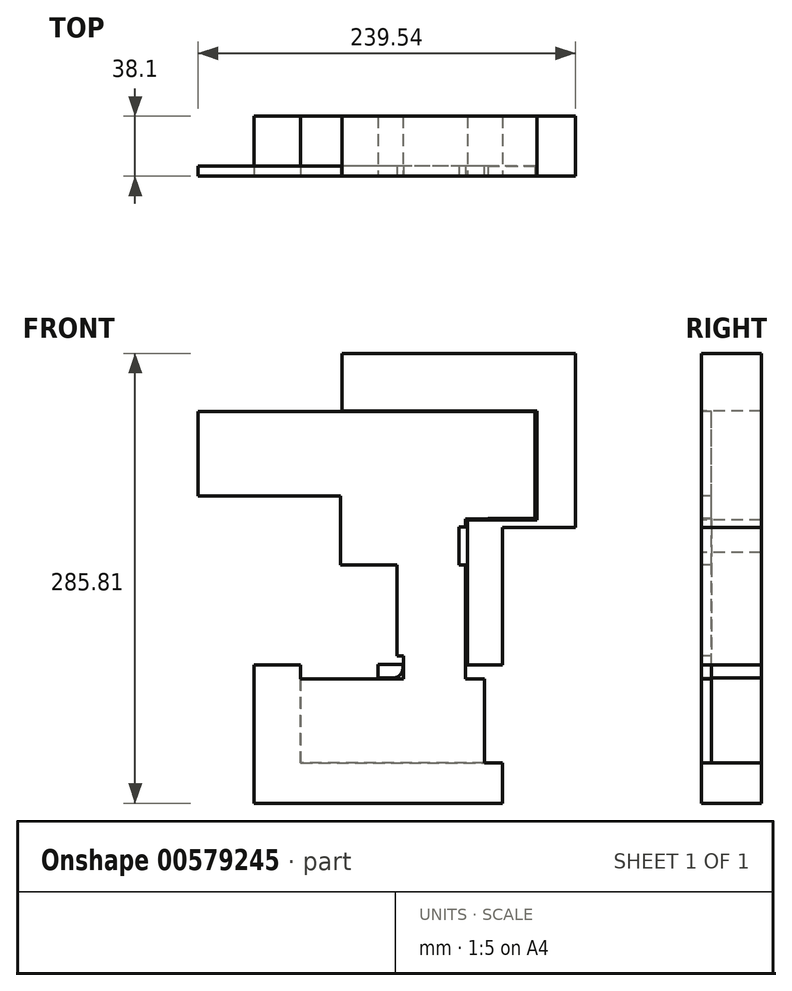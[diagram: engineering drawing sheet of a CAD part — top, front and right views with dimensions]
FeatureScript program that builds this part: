
annotation { "Feature Type Name" : "Feature", "Feature Type Description" : "" }
export const myFeature = defineFeature(function(context is Context, id is Id, definition is map)
    precondition{}
    {
        {
            var Q0;
            Q0=qCreatedBy(makeId("Front.planeOp"),FACE);
            var sketch = newSketch(context, id + "F0", { "sketchPlane" : qUnion([Q0])});
            skLineSegment(sketch, "E0.left", {"start": v(90.58, 112.71) * mm, "end": v(90.58, 180.76) * mm});
            skLineSegment(sketch, "E1.MirrorCS", {"start": v(58.51, 10.86) * mm, "end": v(46.44, 10.86) * mm});
            skLineSegment(sketch, "E2.MirrorCS", {"start": v(46.44, 107.59) * mm, "end": v(42.23, 107.59) * mm});
            skLineSegment(sketch, "E3.MirrorCS", {"start": v(46.44, 112.71) * mm, "end": v(46.44, 107.59) * mm});
            skLineSegment(sketch, "E4.MirrorCS", {"start": v(60.61, 112.71) * mm, "end": v(46.44, 112.46) * mm});
            skLineSegment(sketch, "E5.MirrorCS", {"start": v(42.23, 107.59) * mm, "end": v(46.44, 107.59) * mm});
            skLineSegment(sketch, "E6.MirrorCS", {"start": v(7.13, 10.86) * mm, "end": v(46.44, 10.86) * mm});
            skLineSegment(sketch, "E7.MirrorCS", {"start": v(2.75, 83.2) * mm, "end": v(7.13, 83.2) * mm});
            skLineSegment(sketch, "E8.MirrorCS", {"start": v(46.44, 10.86) * mm, "end": v(7.13, 10.86) * mm});
            skLineSegment(sketch, "E9.MirrorCS", {"start": v(7.13, 25.59) * mm, "end": v(2.75, 25.59) * mm});
            skLineSegment(sketch, "E10.MirrorCS", {"start": v(46.44, 10.86) * mm, "end": v(2.75, 10.86) * mm});
            skLineSegment(sketch, "E11.MirrorCS", {"start": v(7.13, 10.86) * mm, "end": v(7.13, 25.59) * mm});
            skLineSegment(sketch, "E12.MirrorCS", {"start": v(-33.11, 112.71) * mm, "end": v(-33.11, 180.76) * mm});
            skLineSegment(sketch, "E13.MirrorCS", {"start": v(-33.11, 112.71) * mm, "end": v(90.58, 112.71) * mm});
            skLineSegment(sketch, "E14.MirrorCS", {"start": v(-33.11, 127.22) * mm, "end": v(-118.78, 127.22) * mm});
            skLineSegment(sketch, "E15.MirrorCS", {"start": v(2.75, 83.2) * mm, "end": v(-33.11, 83.2) * mm});
            skLineSegment(sketch, "E16.MirrorCS", {"start": v(46.44, 10.86) * mm, "end": v(46.44, 10.86) * mm});
            skLineSegment(sketch, "E17.MirrorCS", {"start": v(2.75, 83.2) * mm, "end": v(2.75, 25.59) * mm});
            skLineSegment(sketch, "E18.MirrorCS", {"start": v(-33.11, 112.71) * mm, "end": v(42.23, 112.71) * mm});
            skLineSegment(sketch, "E19.MirrorCS", {"start": v(90.58, 180.76) * mm, "end": v(-123.38, 180.76) * mm});
            skLineSegment(sketch, "E20.MirrorCS", {"start": v(7.13, 112.46) * mm, "end": v(46.44, 112.46) * mm});
            skLineSegment(sketch, "E21.MirrorCS", {"start": v(-123.38, 127.22) * mm, "end": v(-33.11, 127.22) * mm});
            skLineSegment(sketch, "E22.MirrorCS", {"start": v(-123.38, 127.22) * mm, "end": v(-123.38, 180.76) * mm});
            skLineSegment(sketch, "E23.MirrorCS", {"start": v(-58.33, 10.86) * mm, "end": v(58.51, 10.86) * mm});
            skLineSegment(sketch, "E24.MirrorCS", {"start": v(-58.33, -42.48) * mm, "end": v(-58.33, 10.86) * mm});
            skLineSegment(sketch, "E25.MirrorCS", {"start": v(7.13, 10.86) * mm, "end": v(7.13, 10.86) * mm});
            skLineSegment(sketch, "E26.MirrorCS", {"start": v(-33.11, 83.2) * mm, "end": v(46.44, 83.2) * mm});
            skLineSegment(sketch, "E27.MirrorCS", {"start": v(-33.11, 180.76) * mm, "end": v(-33.11, 112.71) * mm});
            skLineSegment(sketch, "E28.MirrorCS", {"start": v(46.44, 10.86) * mm, "end": v(46.44, 83.2) * mm});
            skLineSegment(sketch, "E29.MirrorCS", {"start": v(46.44, 112.71) * mm, "end": v(2.75, 112.71) * mm});
            skLineSegment(sketch, "E30.MirrorCS", {"start": v(42.23, 112.71) * mm, "end": v(42.23, 83.2) * mm});
            skLineSegment(sketch, "E31.MirrorCS", {"start": v(7.13, 10.86) * mm, "end": v(7.13, 112.46) * mm});
            skLineSegment(sketch, "E32.MirrorCS", {"start": v(-33.11, 83.2) * mm, "end": v(-33.11, 112.71) * mm});
            skLineSegment(sketch, "E33.MirrorCS", {"start": v(-58.33, -42.48) * mm, "end": v(58.51, -42.48) * mm});
            skLineSegment(sketch, "E34", {"start": v(58.51, 10.86) * mm, "end": v(58.51, -42.48) * mm});
            skSolve(sketch);
        }
        {
            var Q0;
            Q0=qCreatedBy(makeId("Front.planeOp"),FACE);
            var sketch = newSketch(context, id + "F1", { "sketchPlane" : qUnion([Q0])});
            skLineSegment(sketch, "E35.bottom", {"start": v(-32.1, 181.22) * mm, "end": v(92.03, 181.22) * mm});
            skLineSegment(sketch, "E35.top", {"start": v(-32.1, 217.68) * mm, "end": v(92.03, 217.68) * mm});
            skLineSegment(sketch, "E35.left", {"start": v(-32.1, 181.22) * mm, "end": v(-32.1, 217.68) * mm});
            skLineSegment(sketch, "E35.right", {"start": v(92.03, 181.22) * mm, "end": v(92.03, 217.68) * mm});
            skLineSegment(sketch, "E36.bottom", {"start": v(47.76, 91.29) * mm, "end": v(69.82, 91.29) * mm});
            skLineSegment(sketch, "E36.top", {"start": v(47.76, 107.02) * mm, "end": v(69.82, 107.02) * mm});
            skLineSegment(sketch, "E36.left", {"start": v(47.76, 91.29) * mm, "end": v(47.76, 107.02) * mm});
            skLineSegment(sketch, "E36.right", {"start": v(69.82, 91.29) * mm, "end": v(69.82, 107.02) * mm});
            skLineSegment(sketch, "E37.bottom", {"start": v(47.72, 19.77) * mm, "end": v(69.82, 19.77) * mm});
            skLineSegment(sketch, "E37.top", {"start": v(47.72, 91.29) * mm, "end": v(69.82, 91.29) * mm});
            skLineSegment(sketch, "E37.left", {"start": v(47.72, 19.77) * mm, "end": v(47.72, 91.29) * mm});
            skLineSegment(sketch, "E37.right", {"start": v(69.82, 19.77) * mm, "end": v(69.82, 91.29) * mm});
            skLineSegment(sketch, "E38.bottom", {"start": v(58.77, 19.77) * mm, "end": v(69.82, 19.77) * mm});
            skLineSegment(sketch, "E38.top", {"start": v(58.77, -42.45) * mm, "end": v(69.82, -42.45) * mm});
            skLineSegment(sketch, "E38.left", {"start": v(58.77, 19.77) * mm, "end": v(58.77, -42.45) * mm});
            skLineSegment(sketch, "E38.right", {"start": v(69.82, 19.77) * mm, "end": v(69.82, -42.45) * mm});
            skLineSegment(sketch, "E39.bottom", {"start": v(69.82, -42.45) * mm, "end": v(-58.3, -42.45) * mm});
            skLineSegment(sketch, "E39.top", {"start": v(69.82, -68.05) * mm, "end": v(-58.3, -68.05) * mm});
            skLineSegment(sketch, "E39.left", {"start": v(69.82, -42.45) * mm, "end": v(69.82, -68.05) * mm});
            skLineSegment(sketch, "E39.right", {"start": v(-58.3, -42.45) * mm, "end": v(-58.3, -68.05) * mm});
            skLineSegment(sketch, "E40.bottom", {"start": v(-58.3, -68.05) * mm, "end": v(-87.9, -68.05) * mm});
            skLineSegment(sketch, "E40.top", {"start": v(-58.3, 19.77) * mm, "end": v(-87.9, 19.77) * mm});
            skLineSegment(sketch, "E40.left", {"start": v(-58.3, -68.05) * mm, "end": v(-58.3, 19.77) * mm});
            skLineSegment(sketch, "E40.right", {"start": v(-87.9, -68.05) * mm, "end": v(-87.9, 19.77) * mm});
            skLineSegment(sketch, "E41.bottom", {"start": v(0.3, 11.52) * mm, "end": v(-9.1, 11.52) * mm});
            skLineSegment(sketch, "E41.top", {"start": v(6.65, 20.04) * mm, "end": v(-9.1, 20.04) * mm});
            skLineSegment(sketch, "E41.left", {"start": v(6.65, 17.87) * mm, "end": v(6.65, 20.04) * mm});
            skLineSegment(sketch, "E41.right", {"start": v(-9.1, 11.52) * mm, "end": v(-9.1, 20.04) * mm});
            skLineSegment(sketch, "E42.bottom", {"start": v(2.21, 20.04) * mm, "end": v(-9.1, 20.04) * mm});
            skLineSegment(sketch, "E42.top", {"start": v(2.21, 76.37) * mm, "end": v(-9.1, 76.37) * mm});
            skLineSegment(sketch, "E42.left", {"start": v(2.21, 20.04) * mm, "end": v(2.21, 76.37) * mm});
            skLineSegment(sketch, "E42.right", {"start": v(-9.1, 20.04) * mm, "end": v(-9.1, 76.37) * mm});
            skLineSegment(sketch, "E43.bottom", {"start": v(-9.1, 11.52) * mm, "end": v(-87.9, 11.52) * mm});
            skLineSegment(sketch, "E43.left", {"start": v(-9.1, 11.52) * mm, "end": v(-9.1, 25.06) * mm});
            skLineSegment(sketch, "E44.bottom", {"start": v(47.67, 107.02) * mm, "end": v(116.16, 107.02) * mm});
            skLineSegment(sketch, "E44.top", {"start": v(47.67, 111.94) * mm, "end": v(116.16, 111.94) * mm});
            skLineSegment(sketch, "E44.left", {"start": v(47.67, 107.02) * mm, "end": v(47.67, 111.94) * mm});
            skLineSegment(sketch, "E44.right", {"start": v(116.16, 107.02) * mm, "end": v(116.16, 111.94) * mm});
            skLineSegment(sketch, "E45.bottom", {"start": v(91.87, 111.94) * mm, "end": v(116.16, 111.94) * mm});
            skLineSegment(sketch, "E45.top", {"start": v(91.87, 217.76) * mm, "end": v(116.16, 217.76) * mm});
            skLineSegment(sketch, "E45.left", {"start": v(91.87, 111.94) * mm, "end": v(91.87, 217.76) * mm});
            skLineSegment(sketch, "E45.right", {"start": v(116.16, 111.94) * mm, "end": v(116.16, 217.76) * mm});
            skLineSegment(sketch, "E46.bottom", {"start": v(116.16, 107.02) * mm, "end": v(69.82, 107.02) * mm});
            skLineSegment(sketch, "E46.top", {"start": v(116.16, -68.05) * mm, "end": v(69.82, -68.05) * mm});
            skLineSegment(sketch, "E46.left", {"start": v(116.16, 107.02) * mm, "end": v(116.16, -68.05) * mm});
            skLineSegment(sketch, "E46.right", {"start": v(69.82, 107.02) * mm, "end": v(69.82, -68.05) * mm});
            skPoint(sketch, "E47.visualSharp", {"position": v(6.65, 11.52) * mm});
            skArc(sketch, "E47.filletArc", {"start": v(0.3, 11.52) * mm, "mid": v(4.79, 13.38) * mm, "end": v(6.65, 17.87) * mm});
            skLineSegment(sketch, "E48", {"start": v(58.77, -42.45) * mm, "end": v(58.77, 19.55) * mm});
            skLineSegment(sketch, "E49.bottom", {"start": v(-9.1, 11.52) * mm, "end": v(-58.3, 11.52) * mm});
            skLineSegment(sketch, "E49.top", {"start": v(-9.1, 19.77) * mm, "end": v(-58.3, 19.77) * mm});
            skLineSegment(sketch, "E49.left", {"start": v(-9.1, 11.52) * mm, "end": v(-9.1, 19.77) * mm});
            skLineSegment(sketch, "E49.right", {"start": v(-58.3, 11.52) * mm, "end": v(-58.3, 19.77) * mm});
            skSolve(sketch);
        }
        {
            var Q0;
            {var subQ0=sQuery(id+"F1.wireOp",EDGE,"E35.left");Q0=makeQuery(id+"F1.imprint","IMPRINT",FACE,{"disambiguationData":[TD([[makeQuery(id+"F1.imprint","IMPRINT",EDGE,{"derivedFrom":subQ0}),-1.0]])]});}
            var Q1;
            {var subQ1=sQuery(id+"F1.wireOp",EDGE,"E42.bottom");Q1=makeQuery(id+"F1.imprint","IMPRINT",FACE,{"disambiguationData":[TD([[makeQuery(id+"F1.imprint","IMPRINT",EDGE,{"derivedFrom":subQ1}),-1.0]])]});}
            var Q2;
            {var subQ1=sQuery(id+"F1.wireOp",EDGE,"E35.right");Q2=makeQuery(id+"F1.imprint","IMPRINT",FACE,{"disambiguationData":[TD([[makeQuery(id+"F1.imprint","IMPRINT",EDGE,{"derivedFrom":subQ1}),-1.0]])]});}
            var Q3;
            {var subQ0=sQuery(id+"F1.wireOp",EDGE,"E35.right");Q3=makeQuery(id+"F1.imprint","IMPRINT",FACE,{"disambiguationData":[TD([[makeQuery(id+"F1.imprint","IMPRINT",EDGE,{"derivedFrom":subQ0}),1.0]])]});}
            var Q4;
            {var subQ1=sQuery(id+"F1.wireOp",EDGE,"E40.bottom");Q4=makeQuery(id+"F1.imprint","IMPRINT",FACE,{"disambiguationData":[TD([[makeQuery(id+"F1.imprint","IMPRINT",EDGE,{"derivedFrom":subQ1}),-1.0]])]});}
            var Q5;
            {var subQ0=sQuery(id+"F1.wireOp",EDGE,"E40.top");Q5=makeQuery(id+"F1.imprint","IMPRINT",FACE,{"disambiguationData":[TD([[makeQuery(id+"F1.imprint","IMPRINT",EDGE,{"derivedFrom":subQ0}),1.0]])]});}
            var Q6;
            Q6=makeQuery(id+"F1.imprint","IMPRINT",FACE,{"disambiguationData":[TD([[makeQuery(id+"F1.imprint","IMPRINT",EDGE,{"derivedFrom":sQuery(id+"F1.wireOp",EDGE,"E41.bottom")}),-1.0]])]});
            var Q7;
            Q7=makeQuery(id+"F1.imprint","IMPRINT",FACE,{"disambiguationData":[TD([[makeQuery(id+"F1.imprint","IMPRINT",EDGE,{"derivedFrom":sQuery(id+"F1.wireOp",EDGE,"E49.bottom")}),-1.0]])]});
            var Q8;
            {var subQ0=sQuery(id+"F1.wireOp",EDGE,"E36.left");Q8=makeQuery(id+"F1.imprint","IMPRINT",FACE,{"disambiguationData":[TD([[makeQuery(id+"F1.imprint","IMPRINT",EDGE,{"derivedFrom":subQ0}),-1.0]])]});}
            var Q9;
            Q9=makeQuery(id+"F1.imprint","IMPRINT",FACE,{"disambiguationData":[TD([[makeQuery(id+"F1.imprint","IMPRINT",EDGE,{"derivedFrom":sQuery(id+"F1.wireOp",EDGE,"E37.bottom")}),1.0]])]});
            var Q10;
            {var subQ1=sQuery(id+"F1.wireOp",EDGE,"E38.bottom");Q10=makeQuery(id+"F1.imprint","IMPRINT",FACE,{"disambiguationData":[TD([[makeQuery(id+"F1.imprint","IMPRINT",EDGE,{"derivedFrom":subQ1}),-1.0]])]});}
            var Q11;
            {var subQ0=sQuery(id+"F1.wireOp",EDGE,"E39.top");Q11=makeQuery(id+"F1.imprint","IMPRINT",FACE,{"disambiguationData":[TD([[makeQuery(id+"F1.imprint","IMPRINT",EDGE,{"derivedFrom":subQ0}),-1.0]])]});}
            var Q12;
            Q12=makeQuery(id+"F1.imprint","IMPRINT",FACE,{"disambiguationData":[TD([[makeQuery(id+"F1.imprint","IMPRINT",EDGE,{"derivedFrom":sQuery(id+"F1.wireOp",EDGE,"E44.top")}),-1.0]])]});
            var Q13;
            {var subQ2=sQuery(id+"F1.wireOp",EDGE,"E46.bottom");Q13=makeQuery(id+"F1.imprint","IMPRINT",FACE,{"disambiguationData":[TD([[makeQuery(id+"F1.imprint","IMPRINT",EDGE,{"derivedFrom":subQ2}),1.0]])]});}
            extrude(context, id + "F2", {"entities" : qUnion([Q0, Q1, Q2, Q3, Q4, Q5, Q6, Q7, Q8, Q9, Q10, Q11, Q12, Q13]), "depth" : -38.1 * mm, "offsetDistance" : 25.4 * mm});
        }
        {
            var Q0;
            Q0=qSketchRegion(id+"F0",true);
            extrude(context, id + "F3", {"entities" : qUnion([Q0]), "operationType" : NewBodyOperationType.ADD, "depth" : -6.35 * mm, "offsetDistance" : 25.4 * mm});
        }
    });
